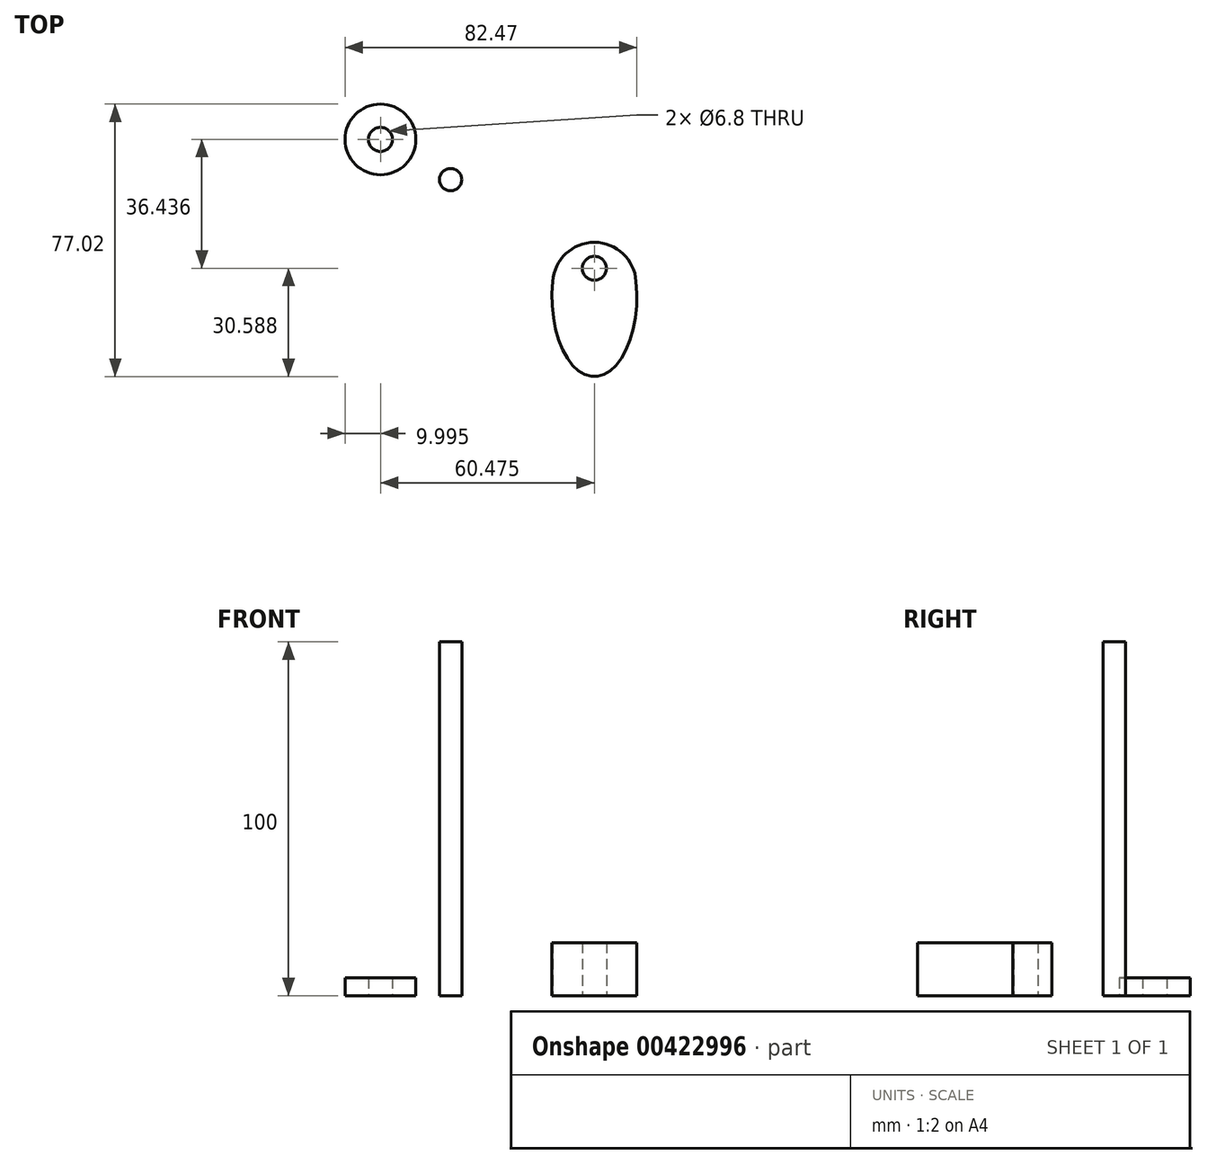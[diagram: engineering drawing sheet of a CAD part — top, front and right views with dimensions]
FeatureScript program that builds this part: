
annotation { "Feature Type Name" : "Feature", "Feature Type Description" : "" }
export const myFeature = defineFeature(function(context is Context, id is Id, definition is map)
    precondition{}
    {
        {
            var Q0;
            Q0=qCreatedBy(makeId("Top.planeOp"),FACE);
            var sketch = newSketch(context, id + "F0", { "sketchPlane" : qUnion([Q0])});
            skArc(sketch, "E0", {"start": v(11.77, 4.4) * mm, "mid": v(0, 15.42) * mm, "end": v(-11.77, 4.4) * mm});
            skEllipticalArc(sketch, "E1", {});
            skCircle(sketch, "E2", {"center": v(0, 8.09) * mm, "radius": 3.4 * mm});
            const initialGuessF0  = {"E1": [0, 0, 0, 1, 0.0225, 0.012, 1.1921220760996334, 5.077588511177399]};
            skSetInitialGuess(sketch, initialGuessF0);
            skSolve(sketch);
        }
        {
            var Q0;
            Q0 = qSketchRegion(id + "F0", true);
            extrude(context, id + "F1", {"entities" : qUnion([Q0]), "depth" : 15 * mm});
        }
        {
            var Q0;
            Q0=qCreatedBy(makeId("Top.planeOp"),FACE);
            var sketch = newSketch(context, id + "F2", { "sketchPlane" : qUnion([Q0])});
            skCircle(sketch, "E3", {"center": v(-60.47, 44.52) * mm, "radius": 10 * mm});
            skCircle(sketch, "E4", {"center": v(-60.47, 44.52) * mm, "radius": 3.4 * mm});
            skSolve(sketch);
        }
        {
            var Q0;
            Q0 = qSketchRegion(id + "F2", true);
            extrude(context, id + "F3", {"entities" : qUnion([Q0]), "depth" : 5 * mm});
        }
        {
            var Q0;
            Q0=qCreatedBy(makeId("Top.planeOp"),FACE);
            var sketch = newSketch(context, id + "F4", { "sketchPlane" : qUnion([Q0])});
            skCircle(sketch, "E5", {"center": v(-40.65, 33.15) * mm, "radius": 3.16 * mm});
            skSolve(sketch);
        }
        {
            var Q0;
            Q0 = qSketchRegion(id + "F4", true);
            extrude(context, id + "F5", {"entities" : qUnion([Q0]), "depth" : 100 * mm});
        }
    });
